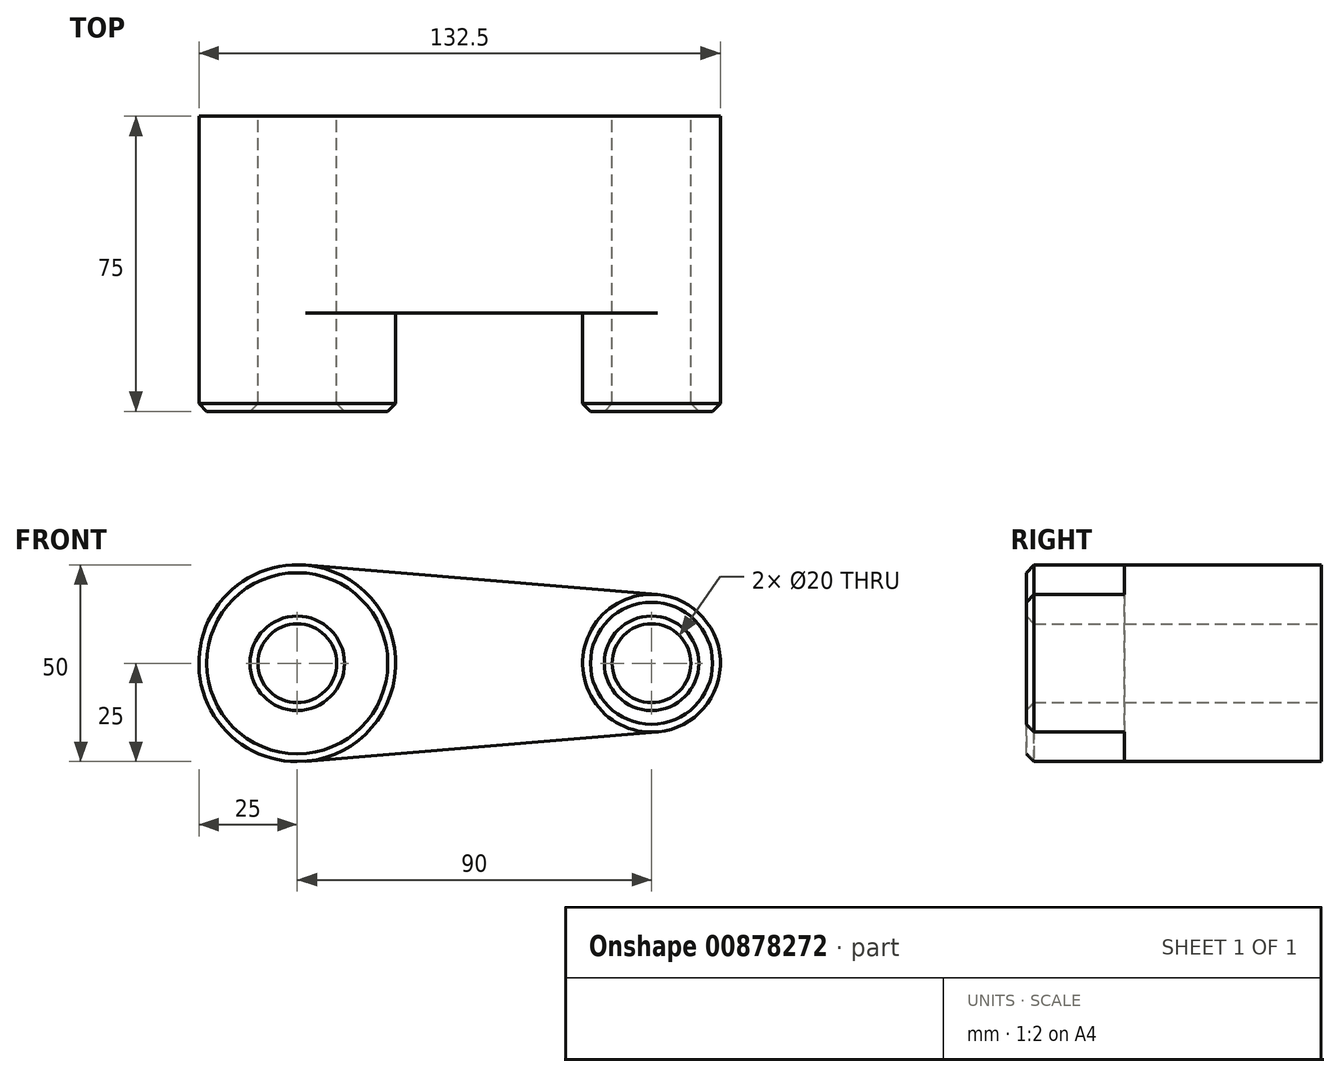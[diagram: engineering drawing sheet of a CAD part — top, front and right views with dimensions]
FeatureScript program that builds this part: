
annotation { "Feature Type Name" : "Feature", "Feature Type Description" : "" }
export const myFeature = defineFeature(function(context is Context, id is Id, definition is map)
    precondition{}
    {
        {
            var Q0;
            Q0=qCreatedBy(makeId("Front.planeOp"),FACE);
            var sketch = newSketch(context, id + "F0", { "sketchPlane" : qUnion([Q0])});
            skCircle(sketch, "E0", {"center": v(0, 0) * mm, "radius": 25 * mm});
            skCircle(sketch, "E1", {"center": v(90, 0) * mm, "radius": 17.5 * mm});
            skCircle(sketch, "E2", {"center": v(0, 0) * mm, "radius": 10 * mm});
            skCircle(sketch, "E3", {"center": v(90, 0) * mm, "radius": 10 * mm});
            skLineSegment(sketch, "E4", {"start": v(2.08, 24.91) * mm, "end": v(91.46, 17.44) * mm});
            skLineSegment(sketch, "E5", {"start": v(2.08, -24.91) * mm, "end": v(91.46, -17.44) * mm});
            skLineSegment(sketch, "E6", {"start": v(91.46, -17.44) * mm, "end": v(2.08, -24.91) * mm});
            skSolve(sketch);
        }
        {
            var Q0;
            {var subQ0=sQuery(id+"F0.wireOp",EDGE,"E4");Q0=makeQuery(id+"F0.imprint","IMPRINT",FACE,{"disambiguationData":[TD([[makeQuery(id+"F0.imprint","IMPRINT",EDGE,{"derivedFrom":subQ0}),-1.0]])]});}
            var Q1;
            Q1=makeQuery(id+"F0.imprint","IMPRINT",FACE,{"disambiguationData":[TD([[makeQuery(id+"F0.imprint","IMPRINT",EDGE,{"derivedFrom":sQuery(id+"F0.wireOp",EDGE,"E2")}),-1.0]])]});
            var Q2;
            Q2=makeQuery(id+"F0.imprint","IMPRINT",FACE,{"disambiguationData":[TD([[makeQuery(id+"F0.imprint","IMPRINT",EDGE,{"derivedFrom":sQuery(id+"F0.wireOp",EDGE,"E3")}),-1.0]])]});
            extrude(context, id + "F1", {"entities" : qUnion([Q0, Q1, Q2]), "depth" : 50 * mm, "offsetDistance" : 25 * mm});
        }
        {
            var Q0;
            Q0=makeQuery(id+"F0.imprint","IMPRINT",FACE,{"disambiguationData":[TD([[makeQuery(id+"F0.imprint","IMPRINT",EDGE,{"derivedFrom":sQuery(id+"F0.wireOp",EDGE,"E2")}),-1.0]])]});
            var Q1;
            Q1=makeQuery(id+"F0.imprint","IMPRINT",FACE,{"disambiguationData":[TD([[makeQuery(id+"F0.imprint","IMPRINT",EDGE,{"derivedFrom":sQuery(id+"F0.wireOp",EDGE,"E3")}),-1.0]])]});
            extrude(context, id + "F2", {"entities" : qUnion([Q0, Q1]), "operationType" : NewBodyOperationType.ADD, "depth" : 75 * mm, "offsetDistance" : 25 * mm});
        }
        {
            var Q0;
            Q0=makeQuery(id+"F2.opExtrude","CAP_EDGE",EDGE,{"disambiguationData":[OSD([sQuery(id+"F0.wireOp",EDGE,"E2")])],"isStart":false});
            var Q1;
            Q1=makeQuery(id+"F2.opExtrude","CAP_EDGE",EDGE,{"disambiguationData":[OSD([sQuery(id+"F0.wireOp",EDGE,"E0")])],"isStart":false});
            var Q2;
            Q2=makeQuery(id+"F2.opExtrude","CAP_EDGE",EDGE,{"disambiguationData":[OSD([sQuery(id+"F0.wireOp",EDGE,"E3")])],"isStart":false});
            var Q3;
            Q3=makeQuery(id+"F2.opExtrude","CAP_EDGE",EDGE,{"disambiguationData":[OSD([sQuery(id+"F0.wireOp",EDGE,"E1")])],"isStart":false});
            chamfer(context, id + "F3", {"entities" : qUnion([Q0, Q1, Q2, Q3]), "width" : 2 * mm, "tangentPropagation" : true});
        }
    });
